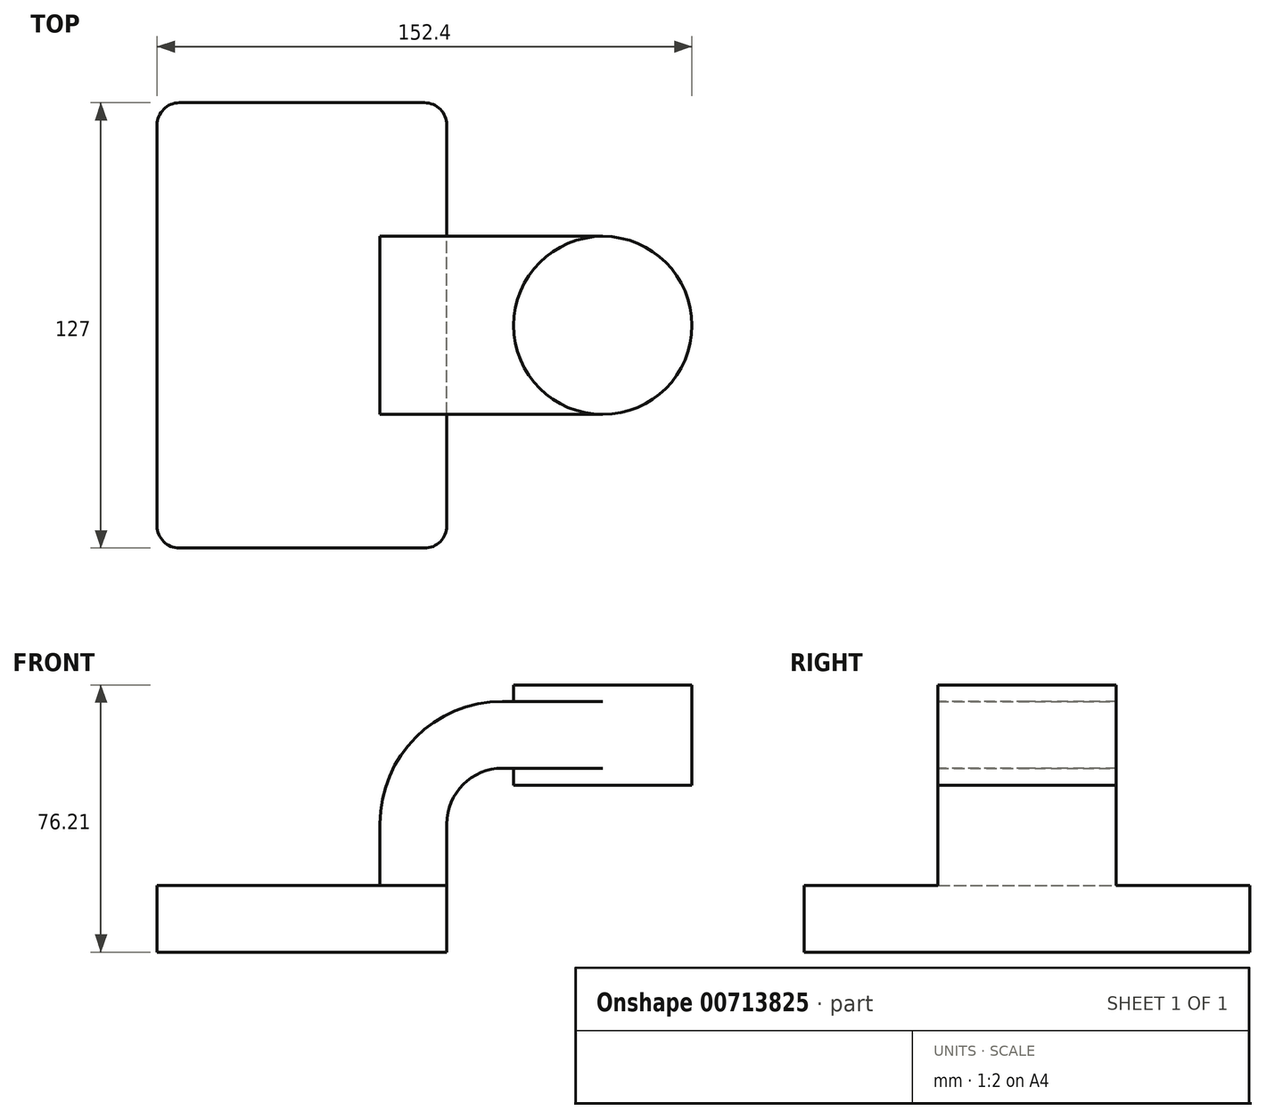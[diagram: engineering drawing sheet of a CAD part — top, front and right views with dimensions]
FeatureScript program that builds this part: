
annotation { "Feature Type Name" : "Feature", "Feature Type Description" : "" }
export const myFeature = defineFeature(function(context is Context, id is Id, definition is map)
    precondition{}
    {
        {
            var Q0;
            Q0=qCreatedBy(makeId("Front.planeOp"),FACE);
            var sketch = newSketch(context, id + "F0", { "sketchPlane" : qUnion([Q0])});
            skLineSegment(sketch, "E0.bottom", {"start": v(-41.28, -9.52) * mm, "end": v(41.28, -9.52) * mm});
            skLineSegment(sketch, "E0.top", {"start": v(-41.28, 9.52) * mm, "end": v(41.28, 9.52) * mm});
            skLineSegment(sketch, "E0.left", {"start": v(-41.28, -9.52) * mm, "end": v(-41.28, 9.52) * mm});
            skLineSegment(sketch, "E0.right", {"start": v(41.28, -9.53) * mm, "end": v(41.28, 9.52) * mm});
            skPoint(sketch, "E0.middle", {"position": v(0, 0) * mm});
            skLineSegment(sketch, "E1.bottom", {"start": v(60.33, 38.1) * mm, "end": v(111.12, 38.1) * mm});
            skLineSegment(sketch, "E1.top", {"start": v(60.33, 66.68) * mm, "end": v(111.12, 66.68) * mm});
            skLineSegment(sketch, "E1.left", {"start": v(60.33, 38.1) * mm, "end": v(60.33, 66.68) * mm});
            skLineSegment(sketch, "E1.right", {"start": v(111.12, 38.1) * mm, "end": v(111.12, 66.68) * mm});
            skPoint(sketch, "E1.middle", {"position": v(85.72, 52.39) * mm});
            skLineSegment(sketch, "E2", {"start": v(41.28, 9.52) * mm, "end": v(41.28, 27.05) * mm});
            skArc(sketch, "E3", {"start": v(41.28, 27.05) * mm, "mid": v(45.92, 38.28) * mm, "end": v(57.15, 42.93) * mm});
            skLineSegment(sketch, "E4", {"start": v(57.15, 42.93) * mm, "end": v(82.07, 42.93) * mm});
            skLineSegment(sketch, "E5.0", {"start": v(57.15, 61.98) * mm, "end": v(82.07, 61.98) * mm});
            skArc(sketch, "E5.1", {"start": v(22.23, 27.05) * mm, "mid": v(32.45, 51.75) * mm, "end": v(57.15, 61.98) * mm});
            skLineSegment(sketch, "E5.2", {"start": v(22.23, 9.52) * mm, "end": v(22.23, 27.05) * mm});
            skLineSegment(sketch, "E6", {"start": v(82.07, 61.98) * mm, "end": v(85.72, 61.98) * mm});
            skPoint(sketch, "E6.endSnap0", {"position": v(85.72, 38.1) * mm});
            skLineSegment(sketch, "E7", {"start": v(82.07, 42.93) * mm, "end": v(85.72, 42.93) * mm});
            skLineSegment(sketch, "E8", {"start": v(85.72, 38.1) * mm, "end": v(85.72, 66.68) * mm});
            skFitSpline(sketch, "E9", {"points": [v(-41.28, 9.53) * mm, v(57.15, 61.98) * mm], "startDerivative": vector(0.1, 102.17) * mm, "endDerivative": vector(112.79, -0.4) * mm});
            skSolve(sketch);
        }
        {
            var Q0;
            Q0=makeQuery(id+"F0.imprint","IMPRINT",FACE,{"disambiguationData":[TD([[makeQuery(id+"F0.imprint","IMPRINT",EDGE,{"derivedFrom":sQuery(id+"F0.wireOp",EDGE,"E0.bottom")}),1.0]])]});
            extrude(context, id + "F1", {"entities" : qUnion([Q0]), "depth" : 127 * mm, "offsetDistance" : 25.4 * mm, "symmetric" : true});
        }
        {
            var Q0;
            {var subQ1=sQuery(id+"F0.wireOp",EDGE,"E2");Q0=makeQuery(id+"F0.imprint","IMPRINT",FACE,{"disambiguationData":[TD([[makeQuery(id+"F0.imprint","IMPRINT",EDGE,{"derivedFrom":subQ1}),1.0]])]});}
            var Q1;
            {var subQ0=sQuery(id+"F0.wireOp",EDGE,"E6");Q1=makeQuery(id+"F0.imprint","IMPRINT",FACE,{"disambiguationData":[TD([[makeQuery(id+"F0.imprint","IMPRINT",EDGE,{"derivedFrom":subQ0}),-1.0]])]});}
            extrude(context, id + "F2", {"entities" : qUnion([Q0, Q1]), "operationType" : NewBodyOperationType.ADD, "depth" : 50.8 * mm, "offsetDistance" : 25.4 * mm, "symmetric" : true});
        }
        {
            var Q0;
            Q0=makeQuery(id+"F0.imprint","IMPRINT",FACE,{"disambiguationData":[TD([[makeQuery(id+"F0.imprint","IMPRINT",EDGE,{"derivedFrom":sQuery(id+"F0.wireOp",EDGE,"E5.1")}),1.0]])]});
            extrude(context, id + "F3", {"entities" : qUnion([Q0]), "operationType" : NewBodyOperationType.ADD, "depth" : 25.4 * mm, "offsetDistance" : 25.4 * mm, "symmetric" : true});
        }
        {
            var Q0;
            {var subQ0=sQuery(id+"F0.wireOp",EDGE,"E1.right");Q0=makeQuery(id+"F0.imprint","IMPRINT",FACE,{"disambiguationData":[TD([[makeQuery(id+"F0.imprint","IMPRINT",EDGE,{"derivedFrom":subQ0}),1.0]])]});}
            var Q1;
            Q1=sQuery(id+"F0.wireOp",EDGE,"E8");
            revolve(context, id + "F4", {"operationType" : NewBodyOperationType.ADD, "surfaceOperationType" : NewSurfaceOperationType.NEW, "entities" : qUnion([Q0]), "axis" : qUnion([Q1]), "revolveType" : RevolveType.FULL});
        }
        {
            var Q0;
            Q0=makeQuery(id+"F1.opExtrude","CAP_EDGE",EDGE,{"disambiguationData":[OSD([sQuery(id+"F0.wireOp",EDGE,"E0.left")])],"isStart":false});
            var Q1;
            Q1=makeQuery(id+"F1.opExtrude","CAP_EDGE",EDGE,{"disambiguationData":[OSD([sQuery(id+"F0.wireOp",EDGE,"E0.right")])],"isStart":false});
            var Q2;
            Q2=makeQuery(id+"F1.opExtrude","CAP_EDGE",EDGE,{"disambiguationData":[OSD([sQuery(id+"F0.wireOp",EDGE,"E0.right")])],"isStart":true});
            var Q3;
            Q3=makeQuery(id+"F1.opExtrude","CAP_EDGE",EDGE,{"disambiguationData":[OSD([sQuery(id+"F0.wireOp",EDGE,"E0.left")])],"isStart":true});
            fillet(context, id + "F5", {"entities" : qUnion([Q0, Q1, Q2, Q3]), "radius" : 6.35 * mm, "tangentPropagation" : true, "allowEdgeOverflow" : false});
        }
    });
